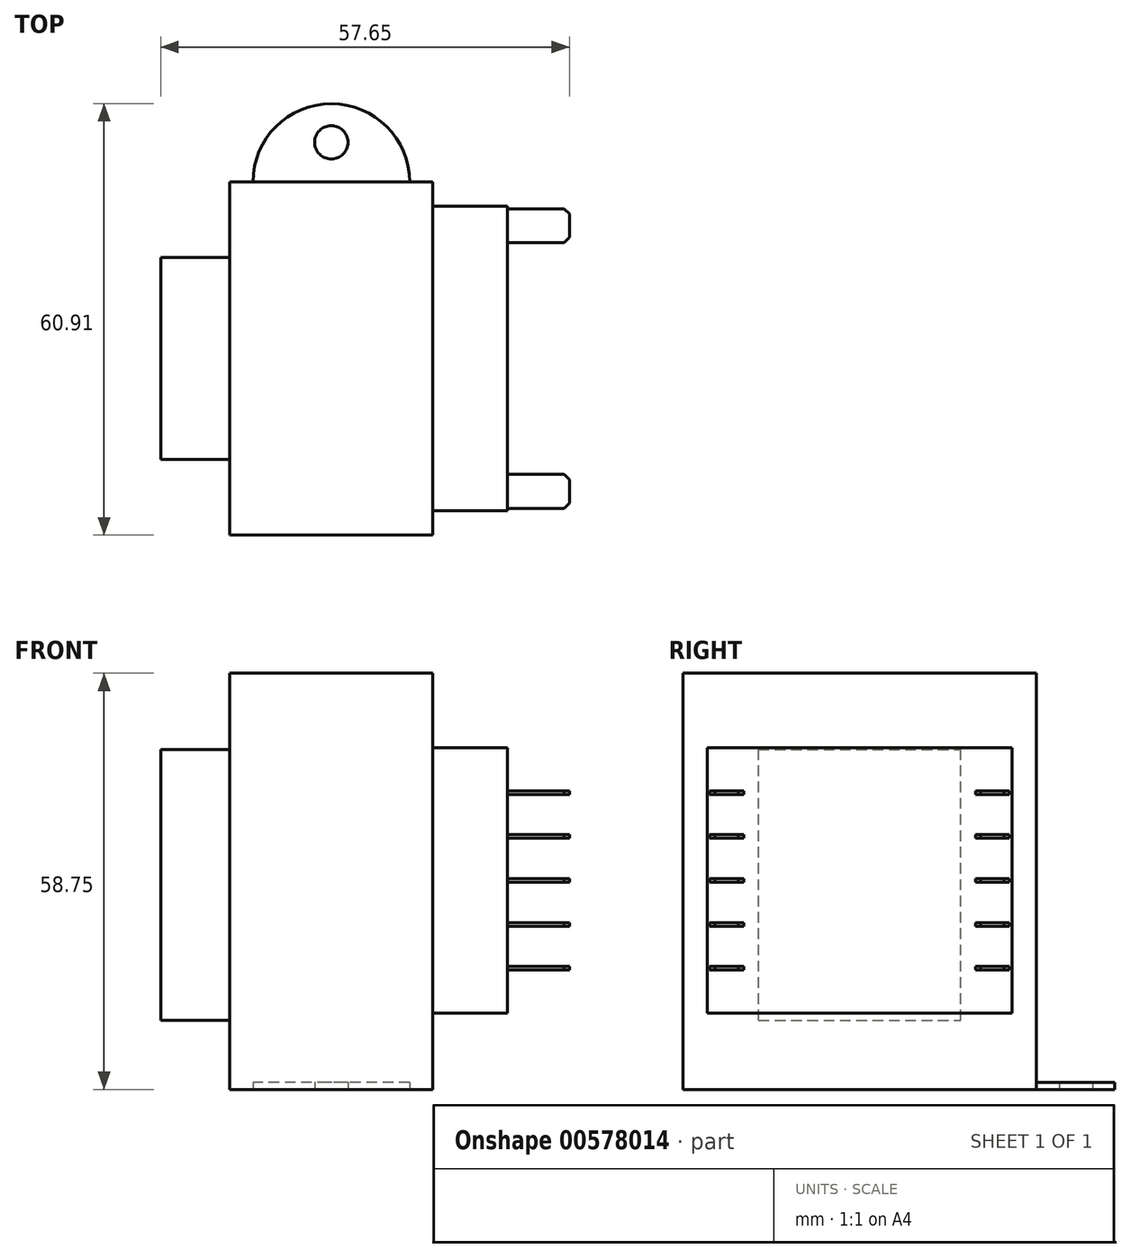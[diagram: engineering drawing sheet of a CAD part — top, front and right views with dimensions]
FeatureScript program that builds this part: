
annotation { "Feature Type Name" : "Feature", "Feature Type Description" : "" }
export const myFeature = defineFeature(function(context is Context, id is Id, definition is map)
    precondition{}
    {
        {
            var Q0;
            Q0=qCreatedBy(makeId("Top.planeOp"),FACE);
            var sketch = newSketch(context, id + "F0", { "sketchPlane" : qUnion([Q0])});
            skLineSegment(sketch, "E0.bottom", {"start": v(14.32, -24.92) * mm, "end": v(-14.32, -24.93) * mm});
            skLineSegment(sketch, "E0.top", {"start": v(14.32, 24.93) * mm, "end": v(-14.33, 24.93) * mm});
            skLineSegment(sketch, "E0.left", {"start": v(14.33, -24.92) * mm, "end": v(14.32, 24.93) * mm});
            skLineSegment(sketch, "E0.right", {"start": v(-14.32, -24.93) * mm, "end": v(-14.33, 24.93) * mm});
            skPoint(sketch, "E0.middle", {"position": v(0, 0) * mm});
            skArc(sketch, "E1", {"start": v(11.05, 24.93) * mm, "mid": v(0, 35.97) * mm, "end": v(-11.05, 24.93) * mm});
            skArc(sketch, "E2.MirrorCS", {"start": v(11.05, -24.93) * mm, "mid": v(0, -35.97) * mm, "end": v(-11.05, -24.93) * mm});
            skCircle(sketch, "E3", {"center": v(0, 30.53) * mm, "radius": 2.35 * mm});
            skCircle(sketch, "E4.MirrorC", {"center": v(0, -30.53) * mm, "radius": 2.35 * mm});
            skSolve(sketch);
        }
        {
            var Q0;
            {var subQ0=sQuery(id+"F0.wireOp",EDGE,"E0.left");Q0=makeQuery(id+"F0.imprint","IMPRINT",FACE,{"disambiguationData":[TD([[makeQuery(id+"F0.imprint","IMPRINT",EDGE,{"derivedFrom":subQ0}),1.0]])]});}
            extrude(context, id + "F1", {"entities" : qUnion([Q0]), "depth" : 58.75 * mm, "offsetDistance" : 25 * mm});
        }
        {
            var Q0;
            {var subQ0=sQuery(id+"F0.wireOp",EDGE,"E2.MirrorCS");Q0=makeQuery(id+"F0.imprint","IMPRINT",FACE,{"disambiguationData":[TD([[makeQuery(id+"F0.imprint","IMPRINT",EDGE,{"derivedFrom":subQ0}),-1.0]])]});}
            var Q1;
            {var subQ0=sQuery(id+"F0.wireOp",EDGE,"E1");Q1=makeQuery(id+"F0.imprint","IMPRINT",FACE,{"disambiguationData":[TD([[makeQuery(id+"F0.imprint","IMPRINT",EDGE,{"derivedFrom":subQ0}),1.0]])]});}
            extrude(context, id + "F2", {"entities" : qUnion([Q0, Q1]), "operationType" : NewBodyOperationType.ADD, "depth" : 1 * mm, "offsetDistance" : 25 * mm});
        }
        {
            var Q0;
            Q0=makeQuery(id+"F1.opExtrude","SWEPT_FACE",FACE,{"disambiguationData":[OSD([sQuery(id+"F0.wireOp",EDGE,"E0.right")])]});
            var sketch = newSketch(context, id + "F3", { "sketchPlane" : qUnion([Q0])});
            skLineSegment(sketch, "E5.bottom", {"start": v(14.25, 9.75) * mm, "end": v(-14.25, 9.75) * mm});
            skLineSegment(sketch, "E5.top", {"start": v(14.25, 48) * mm, "end": v(-14.25, 48) * mm});
            skLineSegment(sketch, "E5.left", {"start": v(14.25, 9.75) * mm, "end": v(14.25, 48) * mm});
            skLineSegment(sketch, "E5.right", {"start": v(-14.25, 9.75) * mm, "end": v(-14.25, 48) * mm});
            skPoint(sketch, "E5.middle", {"position": v(0, 28.88) * mm});
            skSolve(sketch);
        }
        {
            var Q0;
            Q0=makeQuery(id+"F3.imprint","IMPRINT",FACE,{"disambiguationData":[TD([[makeQuery(id+"F3.imprint","IMPRINT",EDGE,{"derivedFrom":sQuery(id+"F3.wireOp",EDGE,"E5.bottom")}),-1.0]])]});
            extrude(context, id + "F4", {"entities" : qUnion([Q0]), "operationType" : NewBodyOperationType.ADD, "depth" : 9.75 * mm, "offsetDistance" : 25 * mm});
        }
        {
            var Q0;
            Q0=makeQuery(id+"F1.opExtrude","SWEPT_FACE",FACE,{"disambiguationData":[OSD([sQuery(id+"F0.wireOp",EDGE,"E0.left")])]});
            var sketch = newSketch(context, id + "F5", { "sketchPlane" : qUnion([Q0])});
            skLineSegment(sketch, "E6.bottom", {"start": v(21.5, 10.75) * mm, "end": v(-21.5, 10.75) * mm});
            skLineSegment(sketch, "E6.top", {"start": v(21.5, 48.25) * mm, "end": v(-21.5, 48.25) * mm});
            skLineSegment(sketch, "E6.left", {"start": v(21.5, 10.75) * mm, "end": v(21.5, 48.25) * mm});
            skLineSegment(sketch, "E6.right", {"start": v(-21.5, 10.75) * mm, "end": v(-21.5, 48.25) * mm});
            skPoint(sketch, "E6.middle", {"position": v(0, 29.5) * mm});
            skSolve(sketch);
        }
        {
            var Q0;
            Q0=makeQuery(id+"F5.imprint","IMPRINT",FACE,{"disambiguationData":[TD([[makeQuery(id+"F5.imprint","IMPRINT",EDGE,{"derivedFrom":sQuery(id+"F5.wireOp",EDGE,"E6.bottom")}),-1.0]])]});
            extrude(context, id + "F6", {"entities" : qUnion([Q0]), "operationType" : NewBodyOperationType.ADD, "depth" : 10.5 * mm, "offsetDistance" : 25 * mm});
        }
        {
            var Q0;
            Q0=makeQuery(id+"F6.opExtrude","CAP_FACE",FACE,{"disambiguationData":[OSD([sQuery(id+"F5.wireOp",EDGE,"E6.bottom"),sQuery(id+"F5.wireOp",EDGE,"E6.top"),sQuery(id+"F5.wireOp",EDGE,"E6.left"),sQuery(id+"F5.wireOp",EDGE,"E6.right")])],"isStart":false});
            var sketch = newSketch(context, id + "F7", { "sketchPlane" : qUnion([Q0])});
            skLineSegment(sketch, "E7", {"start": v(21.5, 29.5) * mm, "end": v(-21.5, 29.5) * mm, "construction": true});
            skLineSegment(sketch, "E8.bottom", {"start": v(-16.35, 29.25) * mm, "end": v(-21.15, 29.25) * mm});
            skLineSegment(sketch, "E8.top", {"start": v(-16.35, 29.75) * mm, "end": v(-21.15, 29.75) * mm});
            skLineSegment(sketch, "E8.left", {"start": v(-16.35, 29.25) * mm, "end": v(-16.35, 29.75) * mm});
            skLineSegment(sketch, "E8.right", {"start": v(-21.15, 29.25) * mm, "end": v(-21.15, 29.75) * mm});
            skPoint(sketch, "E8.middle", {"position": v(-18.75, 29.5) * mm});
            skLineSegment(sketch, "E9.1.0.0", {"start": v(-16.35, 35.95) * mm, "end": v(-21.15, 35.95) * mm});
            skLineSegment(sketch, "E9.1.0.1", {"start": v(-21.15, 35.45) * mm, "end": v(-21.15, 35.95) * mm});
            skLineSegment(sketch, "E9.1.0.2", {"start": v(-16.35, 35.45) * mm, "end": v(-21.15, 35.45) * mm});
            skLineSegment(sketch, "E9.1.0.3", {"start": v(-16.35, 35.45) * mm, "end": v(-16.35, 35.95) * mm});
            skLineSegment(sketch, "E9.2.0.0", {"start": v(-16.35, 42.15) * mm, "end": v(-21.15, 42.15) * mm});
            skLineSegment(sketch, "E9.2.0.1", {"start": v(-21.15, 41.65) * mm, "end": v(-21.15, 42.15) * mm});
            skLineSegment(sketch, "E9.2.0.2", {"start": v(-16.35, 41.65) * mm, "end": v(-21.15, 41.65) * mm});
            skLineSegment(sketch, "E9.2.0.3", {"start": v(-16.35, 41.65) * mm, "end": v(-16.35, 42.15) * mm});
            skLineSegment(sketch, "E9.direction1", {"start": v(-21.15, 29.75) * mm, "end": v(-21.15, 35.95) * mm, "construction": true});
            skLineSegment(sketch, "E10.MirrorCS", {"start": v(-16.35, 16.85) * mm, "end": v(-21.15, 16.85) * mm});
            skLineSegment(sketch, "E11.MirrorCS", {"start": v(-16.35, 17.35) * mm, "end": v(-21.15, 17.35) * mm});
            skLineSegment(sketch, "E12.MirrorCS", {"start": v(-16.35, 17.35) * mm, "end": v(-16.35, 16.85) * mm});
            skLineSegment(sketch, "E13.MirrorCS", {"start": v(-21.15, 17.35) * mm, "end": v(-21.15, 16.85) * mm});
            skLineSegment(sketch, "E14.MirrorCS", {"start": v(-16.35, 23.05) * mm, "end": v(-21.15, 23.05) * mm});
            skLineSegment(sketch, "E15.MirrorCS", {"start": v(-21.15, 29.25) * mm, "end": v(-21.15, 23.05) * mm, "construction": true});
            skLineSegment(sketch, "E16.MirrorCS", {"start": v(-16.35, 23.55) * mm, "end": v(-21.15, 23.55) * mm});
            skLineSegment(sketch, "E17.MirrorCS", {"start": v(-16.35, 23.55) * mm, "end": v(-16.35, 23.05) * mm});
            skLineSegment(sketch, "E18.MirrorCS", {"start": v(21.15, 29.25) * mm, "end": v(21.15, 29.75) * mm});
            skLineSegment(sketch, "E19.MirrorCS", {"start": v(21.15, 35.45) * mm, "end": v(21.15, 35.95) * mm});
            skLineSegment(sketch, "E20.MirrorCS", {"start": v(21.15, 17.35) * mm, "end": v(21.15, 16.85) * mm});
            skLineSegment(sketch, "E21.MirrorCS", {"start": v(16.35, 23.55) * mm, "end": v(16.35, 23.05) * mm});
            skLineSegment(sketch, "E22.MirrorCS", {"start": v(16.35, 29.25) * mm, "end": v(16.35, 29.75) * mm});
            skLineSegment(sketch, "E23.MirrorCS", {"start": v(16.35, 35.45) * mm, "end": v(16.35, 35.95) * mm});
            skLineSegment(sketch, "E24.MirrorCS", {"start": v(21.15, 41.65) * mm, "end": v(21.15, 42.15) * mm});
            skLineSegment(sketch, "E25.MirrorCS", {"start": v(16.35, 17.35) * mm, "end": v(16.35, 16.85) * mm});
            skLineSegment(sketch, "E26.MirrorCS", {"start": v(16.35, 41.65) * mm, "end": v(16.35, 42.15) * mm});
            skLineSegment(sketch, "E27.MirrorCS", {"start": v(21.15, 29.25) * mm, "end": v(21.15, 23.05) * mm, "construction": true});
            skLineSegment(sketch, "E28.MirrorCS", {"start": v(21.15, 29.75) * mm, "end": v(21.15, 35.95) * mm, "construction": true});
            skPoint(sketch, "E29.MirrorP", {"position": v(18.75, 29.5) * mm});
            skLineSegment(sketch, "E30.MirrorCS", {"start": v(16.35, 16.85) * mm, "end": v(21.15, 16.85) * mm});
            skLineSegment(sketch, "E31.MirrorCS", {"start": v(16.35, 17.35) * mm, "end": v(21.15, 17.35) * mm});
            skLineSegment(sketch, "E32.MirrorCS", {"start": v(-21.5, 29.5) * mm, "end": v(21.5, 29.5) * mm, "construction": true});
            skLineSegment(sketch, "E33.MirrorCS", {"start": v(16.35, 29.25) * mm, "end": v(21.15, 29.25) * mm});
            skLineSegment(sketch, "E34.MirrorCS", {"start": v(16.35, 29.75) * mm, "end": v(21.15, 29.75) * mm});
            skLineSegment(sketch, "E35.MirrorCS", {"start": v(16.35, 35.45) * mm, "end": v(21.15, 35.45) * mm});
            skLineSegment(sketch, "E36.MirrorCS", {"start": v(16.35, 23.55) * mm, "end": v(21.15, 23.55) * mm});
            skLineSegment(sketch, "E37.MirrorCS", {"start": v(16.35, 23.05) * mm, "end": v(21.15, 23.05) * mm});
            skLineSegment(sketch, "E38.MirrorCS", {"start": v(16.35, 35.95) * mm, "end": v(21.15, 35.95) * mm});
            skLineSegment(sketch, "E39.MirrorCS", {"start": v(16.35, 42.15) * mm, "end": v(21.15, 42.15) * mm});
            skLineSegment(sketch, "E40.MirrorCS", {"start": v(16.35, 41.65) * mm, "end": v(21.15, 41.65) * mm});
            skLineSegment(sketch, "E41", {"start": v(-21.15, 23.55) * mm, "end": v(-21.15, 23.05) * mm});
            skLineSegment(sketch, "E42", {"start": v(21.15, 23.55) * mm, "end": v(21.15, 23.05) * mm});
            skSolve(sketch);
        }
        {
            var Q0;
            Q0 = qSketchRegion(id + "F7", true);
            extrude(context, id + "F8", {"entities" : qUnion([Q0]), "operationType" : NewBodyOperationType.ADD, "depth" : 8.75 * mm, "offsetDistance" : 25 * mm});
        }
        {
            var Q0;
            Q0=makeQuery(id+"F8.opExtrude","CAP_EDGE",EDGE,{"disambiguationData":[OSD([sQuery(id+"F7.wireOp",EDGE,"E9.2.0.1")])],"isStart":false});
            var Q1;
            Q1=makeQuery(id+"F8.opExtrude","CAP_EDGE",EDGE,{"disambiguationData":[OSD([sQuery(id+"F7.wireOp",EDGE,"E9.2.0.3")])],"isStart":false});
            var Q2;
            Q2=makeQuery(id+"F8.opExtrude","CAP_EDGE",EDGE,{"disambiguationData":[OSD([sQuery(id+"F7.wireOp",EDGE,"E9.1.0.1")])],"isStart":false});
            var Q3;
            Q3=makeQuery(id+"F8.opExtrude","CAP_EDGE",EDGE,{"disambiguationData":[OSD([sQuery(id+"F7.wireOp",EDGE,"E9.1.0.3")])],"isStart":false});
            var Q4;
            Q4=makeQuery(id+"F8.opExtrude","CAP_EDGE",EDGE,{"disambiguationData":[OSD([sQuery(id+"F7.wireOp",EDGE,"E8.right")])],"isStart":false});
            var Q5;
            Q5=makeQuery(id+"F8.opExtrude","CAP_EDGE",EDGE,{"disambiguationData":[OSD([sQuery(id+"F7.wireOp",EDGE,"E8.left")])],"isStart":false});
            var Q6;
            Q6=makeQuery(id+"F8.opExtrude","CAP_EDGE",EDGE,{"disambiguationData":[OSD([sQuery(id+"F7.wireOp",EDGE,"E13.MirrorCS")])],"isStart":false});
            var Q7;
            Q7=makeQuery(id+"F8.opExtrude","CAP_EDGE",EDGE,{"disambiguationData":[OSD([sQuery(id+"F7.wireOp",EDGE,"E12.MirrorCS")])],"isStart":false});
            var Q8;
            Q8=makeQuery(id+"F8.opExtrude","CAP_EDGE",EDGE,{"disambiguationData":[OSD([sQuery(id+"F7.wireOp",EDGE,"E25.MirrorCS")])],"isStart":false});
            var Q9;
            Q9=makeQuery(id+"F8.opExtrude","CAP_EDGE",EDGE,{"disambiguationData":[OSD([sQuery(id+"F7.wireOp",EDGE,"E20.MirrorCS")])],"isStart":false});
            var Q10;
            Q10=makeQuery(id+"F8.opExtrude","CAP_EDGE",EDGE,{"disambiguationData":[OSD([sQuery(id+"F7.wireOp",EDGE,"E22.MirrorCS")])],"isStart":false});
            var Q11;
            Q11=makeQuery(id+"F8.opExtrude","CAP_EDGE",EDGE,{"disambiguationData":[OSD([sQuery(id+"F7.wireOp",EDGE,"E18.MirrorCS")])],"isStart":false});
            var Q12;
            Q12=makeQuery(id+"F8.opExtrude","CAP_EDGE",EDGE,{"disambiguationData":[OSD([sQuery(id+"F7.wireOp",EDGE,"E23.MirrorCS")])],"isStart":false});
            var Q13;
            Q13=makeQuery(id+"F8.opExtrude","CAP_EDGE",EDGE,{"disambiguationData":[OSD([sQuery(id+"F7.wireOp",EDGE,"E19.MirrorCS")])],"isStart":false});
            var Q14;
            Q14=makeQuery(id+"F8.opExtrude","CAP_EDGE",EDGE,{"disambiguationData":[OSD([sQuery(id+"F7.wireOp",EDGE,"E26.MirrorCS")])],"isStart":false});
            var Q15;
            Q15=makeQuery(id+"F8.opExtrude","CAP_EDGE",EDGE,{"disambiguationData":[OSD([sQuery(id+"F7.wireOp",EDGE,"E24.MirrorCS")])],"isStart":false});
            var Q16;
            Q16=makeQuery(id+"F8.opExtrude","CAP_EDGE",EDGE,{"disambiguationData":[OSD([sQuery(id+"F7.wireOp",EDGE,"E17.MirrorCS")])],"isStart":false});
            var Q17;
            Q17=makeQuery(id+"F8.opExtrude","CAP_EDGE",EDGE,{"disambiguationData":[OSD([sQuery(id+"F7.wireOp",EDGE,"E41")])],"isStart":false});
            var Q18;
            Q18=makeQuery(id+"F8.opExtrude","CAP_EDGE",EDGE,{"disambiguationData":[OSD([sQuery(id+"F7.wireOp",EDGE,"E21.MirrorCS")])],"isStart":false});
            var Q19;
            Q19=makeQuery(id+"F8.opExtrude","CAP_EDGE",EDGE,{"disambiguationData":[OSD([sQuery(id+"F7.wireOp",EDGE,"E42")])],"isStart":false});
            chamfer(context, id + "F9", {"entities" : qUnion([Q0, Q1, Q2, Q3, Q4, Q5, Q6, Q7, Q8, Q9, Q10, Q11, Q12, Q13, Q14, Q15, Q16, Q17, Q18, Q19]), "width" : 0.75 * mm, "tangentPropagation" : true});
        }
    });
